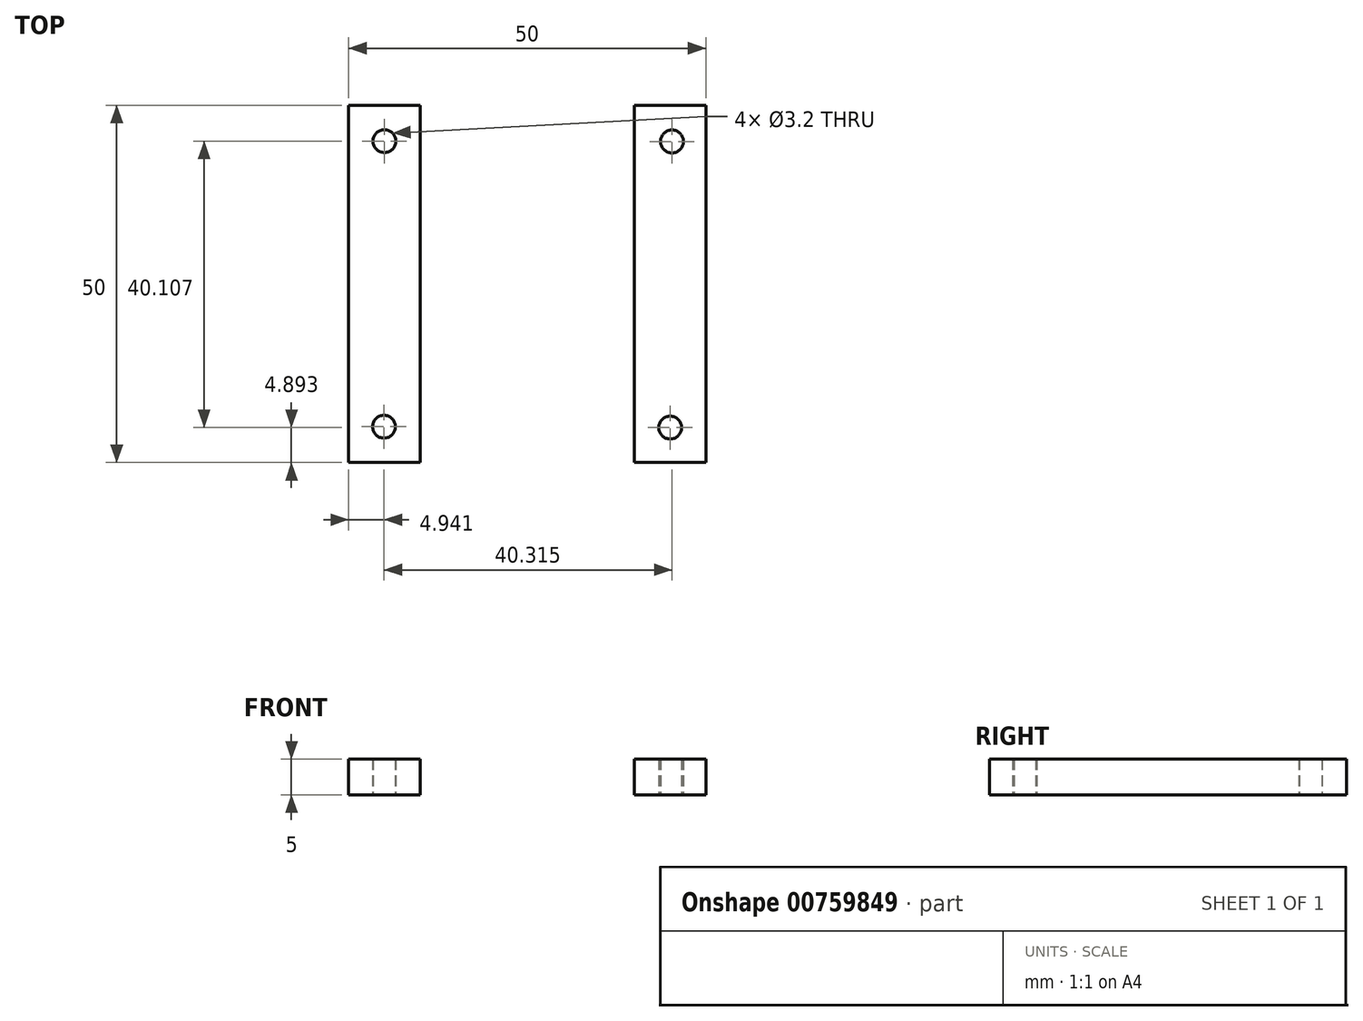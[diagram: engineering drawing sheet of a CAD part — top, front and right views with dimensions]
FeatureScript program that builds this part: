
annotation { "Feature Type Name" : "Feature", "Feature Type Description" : "" }
export const myFeature = defineFeature(function(context is Context, id is Id, definition is map)
    precondition{}
    {
        {
            var Q0;
            Q0=qCreatedBy(makeId("Top.planeOp"),FACE);
            var sketch = newSketch(context, id + "F0", { "sketchPlane" : qUnion([Q0])});
            skLineSegment(sketch, "E0.bottom", {"start": v(-27.5, 25) * mm, "end": v(27.5, 25) * mm});
            skLineSegment(sketch, "E0.top", {"start": v(-27.5, -25) * mm, "end": v(27.5, -25) * mm});
            skLineSegment(sketch, "E0.left", {"start": v(-27.5, 25) * mm, "end": v(-27.5, -25) * mm});
            skLineSegment(sketch, "E0.right", {"start": v(27.5, 25) * mm, "end": v(27.5, -25) * mm});
            skPoint(sketch, "E0.middle", {"position": v(0, 0) * mm});
            skLineSegment(sketch, "E1.bottom", {"start": v(-20, 20) * mm, "end": v(20, 20) * mm, "construction": true});
            skLineSegment(sketch, "E1.top", {"start": v(-20, -20) * mm, "end": v(20, -20) * mm, "construction": true});
            skLineSegment(sketch, "E1.left", {"start": v(-20, 20) * mm, "end": v(-20, -20) * mm, "construction": true});
            skLineSegment(sketch, "E1.right", {"start": v(20, 20) * mm, "end": v(20, -20) * mm, "construction": true});
            skCircle(sketch, "E2", {"center": v(-20, 20) * mm, "radius": 1.6 * mm});
            skCircle(sketch, "E3", {"center": v(-20.06, -19.99) * mm, "radius": 1.6 * mm});
            skCircle(sketch, "E4", {"center": v(20, -20.11) * mm, "radius": 1.6 * mm});
            skCircle(sketch, "E5", {"center": v(20.25, 19.94) * mm, "radius": 1.6 * mm});
            skLineSegment(sketch, "E6.top", {"start": v(-83.24, -25) * mm, "end": v(-33.24, -25) * mm});
            skLineSegment(sketch, "E6.left", {"start": v(-83.24, 25) * mm, "end": v(-83.24, -25) * mm});
            skLineSegment(sketch, "E6.right", {"start": v(-33.24, 25) * mm, "end": v(-33.24, -25) * mm});
            skPoint(sketch, "E6.middle", {"position": v(-58.24, 0) * mm});
            skLineSegment(sketch, "E7.bottom", {"start": v(-78.24, 20) * mm, "end": v(-38.24, 20) * mm, "construction": true});
            skLineSegment(sketch, "E7.top", {"start": v(-78.24, -20) * mm, "end": v(-38.24, -20) * mm, "construction": true});
            skLineSegment(sketch, "E7.left", {"start": v(-78.24, 20) * mm, "end": v(-78.24, -20) * mm, "construction": true});
            skLineSegment(sketch, "E7.right", {"start": v(-38.24, 20) * mm, "end": v(-38.24, -20) * mm, "construction": true});
            skCircle(sketch, "E8", {"center": v(-78.24, 20) * mm, "radius": 1.6 * mm});
            skCircle(sketch, "E9", {"center": v(-78.3, -19.98) * mm, "radius": 1.6 * mm});
            skCircle(sketch, "E10", {"center": v(-38.24, -20.1) * mm, "radius": 1.6 * mm});
            skCircle(sketch, "E11", {"center": v(-37.98, 19.95) * mm, "radius": 1.6 * mm});
            skLineSegment(sketch, "E12.bottom", {"start": v(-83.24, -25) * mm, "end": v(-73.24, -25) * mm});
            skLineSegment(sketch, "E12.top", {"start": v(-83.24, 25) * mm, "end": v(-73.24, 25) * mm});
            skLineSegment(sketch, "E12.left", {"start": v(-83.24, -25) * mm, "end": v(-83.24, 25) * mm});
            skLineSegment(sketch, "E12.right", {"start": v(-73.24, -25) * mm, "end": v(-73.24, 25) * mm});
            skLineSegment(sketch, "E13.bottom", {"start": v(-33.24, 25) * mm, "end": v(-43.24, 25) * mm});
            skLineSegment(sketch, "E13.top", {"start": v(-33.24, -25) * mm, "end": v(-43.24, -25) * mm});
            skLineSegment(sketch, "E13.right", {"start": v(-43.24, 25) * mm, "end": v(-43.24, -25) * mm});
            skLineSegment(sketch, "E14.left", {"start": v(-83.24, 25) * mm, "end": v(-83.24, 45) * mm});
            skLineSegment(sketch, "E14.right", {"start": v(-33.24, 25) * mm, "end": v(-33.24, 45) * mm});
            skLineSegment(sketch, "E15.top", {"start": v(-27.5, 45) * mm, "end": v(27.5, 45) * mm});
            skLineSegment(sketch, "E15.left", {"start": v(-27.5, 25) * mm, "end": v(-27.5, 45) * mm});
            skLineSegment(sketch, "E15.right", {"start": v(27.5, 25) * mm, "end": v(27.5, 45) * mm});
            skLineSegment(sketch, "E16.bottom", {"start": v(-73.24, 25) * mm, "end": v(-83.24, 25) * mm});
            skLineSegment(sketch, "E16.top", {"start": v(-73.24, 45) * mm, "end": v(-83.24, 45) * mm});
            skLineSegment(sketch, "E16.left", {"start": v(-73.24, 25) * mm, "end": v(-73.24, 45) * mm});
            skLineSegment(sketch, "E17.bottom", {"start": v(-43.24, 25) * mm, "end": v(-33.24, 25) * mm});
            skLineSegment(sketch, "E17.top", {"start": v(-43.24, 45) * mm, "end": v(-33.24, 45) * mm});
            skLineSegment(sketch, "E17.left", {"start": v(-43.24, 25) * mm, "end": v(-43.24, 45) * mm});
            skLineSegment(sketch, "E18.bottom", {"start": v(37.36, 24.81) * mm, "end": v(92.36, 24.81) * mm});
            skLineSegment(sketch, "E18.top", {"start": v(37.36, -25.19) * mm, "end": v(92.36, -25.19) * mm});
            skLineSegment(sketch, "E18.left", {"start": v(37.36, 24.81) * mm, "end": v(37.36, -25.19) * mm});
            skLineSegment(sketch, "E18.right", {"start": v(92.36, 24.81) * mm, "end": v(92.36, -25.19) * mm});
            skPoint(sketch, "E18.middle", {"position": v(64.86, -0.19) * mm});
            skLineSegment(sketch, "E19.bottom", {"start": v(44.86, 19.81) * mm, "end": v(84.86, 19.81) * mm, "construction": true});
            skLineSegment(sketch, "E19.top", {"start": v(44.86, -20.19) * mm, "end": v(84.86, -20.19) * mm, "construction": true});
            skLineSegment(sketch, "E19.left", {"start": v(44.86, 19.81) * mm, "end": v(44.86, -20.19) * mm, "construction": true});
            skLineSegment(sketch, "E19.right", {"start": v(84.86, 19.81) * mm, "end": v(84.86, -20.19) * mm, "construction": true});
            skCircle(sketch, "E20", {"center": v(44.86, 19.81) * mm, "radius": 1.6 * mm});
            skCircle(sketch, "E21", {"center": v(44.8, -20.17) * mm, "radius": 1.6 * mm});
            skCircle(sketch, "E22", {"center": v(84.86, -20.3) * mm, "radius": 1.6 * mm});
            skCircle(sketch, "E23", {"center": v(85.11, 19.76) * mm, "radius": 1.6 * mm});
            skLineSegment(sketch, "E24.top", {"start": v(37.36, 44.81) * mm, "end": v(92.36, 44.81) * mm});
            skLineSegment(sketch, "E24.left", {"start": v(37.36, 24.81) * mm, "end": v(37.36, 44.81) * mm});
            skLineSegment(sketch, "E24.right", {"start": v(92.36, 24.81) * mm, "end": v(92.36, 44.81) * mm});
            skCircle(sketch, "E25", {"center": v(64.86, -0.19) * mm, "radius": 15 * mm});
            skLineSegment(sketch, "E26.bottom", {"start": v(-12.25, 13.66) * mm, "end": v(12.75, 13.66) * mm});
            skLineSegment(sketch, "E26.top", {"start": v(-12.25, 12.66) * mm, "end": v(12.75, 12.66) * mm});
            skLineSegment(sketch, "E26.left", {"start": v(-12.25, 13.66) * mm, "end": v(-12.25, 12.66) * mm});
            skLineSegment(sketch, "E26.right", {"start": v(12.75, 13.66) * mm, "end": v(12.75, 12.66) * mm});
            skSolve(sketch);
        }
        {
            var Q0;
            Q0=makeQuery(id+"F0.imprint","IMPRINT",FACE,{"disambiguationData":[TD([[makeQuery(id+"F0.imprint","IMPRINT",EDGE,{"derivedFrom":sQuery(id+"F0.wireOp",EDGE,"E8")}),-1.0]])]});
            var Q1;
            Q1=makeQuery(id+"F0.imprint","IMPRINT",FACE,{"disambiguationData":[TD([[makeQuery(id+"F0.imprint","IMPRINT",EDGE,{"derivedFrom":sQuery(id+"F0.wireOp",EDGE,"E10")}),-1.0]])]});
            extrude(context, id + "F1", {"entities" : qUnion([Q0, Q1]), "depth" : 5 * mm, "offsetDistance" : 25 * mm});
        }
    });
